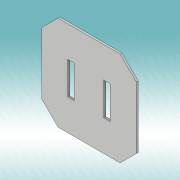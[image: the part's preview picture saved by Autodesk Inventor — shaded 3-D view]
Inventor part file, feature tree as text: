
AUTODESK INVENTOR PART (.ipt)
format: ipt  version: 2019 (Build 230136000, 136)  size: 117,248 bytes
history: native  units: mm
features: extrude x2, sketch x2
ambient origin geometry x8: Origin, YZ Plane, XZ Plane, XY Plane, X Axis, Y Axis, Z Axis, Center Point
bodies: Solid1 (feature_tree)
feature tree (4):
  extrude  "Extrusion1"  Depth=47.5mm
  extrude  "Extrusion2"  Depth=3.0mm TaperAngle=0.0deg
  sketch  "Sketch1"  dims[d0=47.5mm d2=35.0mm]
  sketch  "Sketch2"  dims[d3=135.0deg d4=3.0mm d5=0.0mm d6=50.0mm d7=10.0mm d8=45.0mm d10=47.5mm d11=3.0mm d12=0.0mm]
